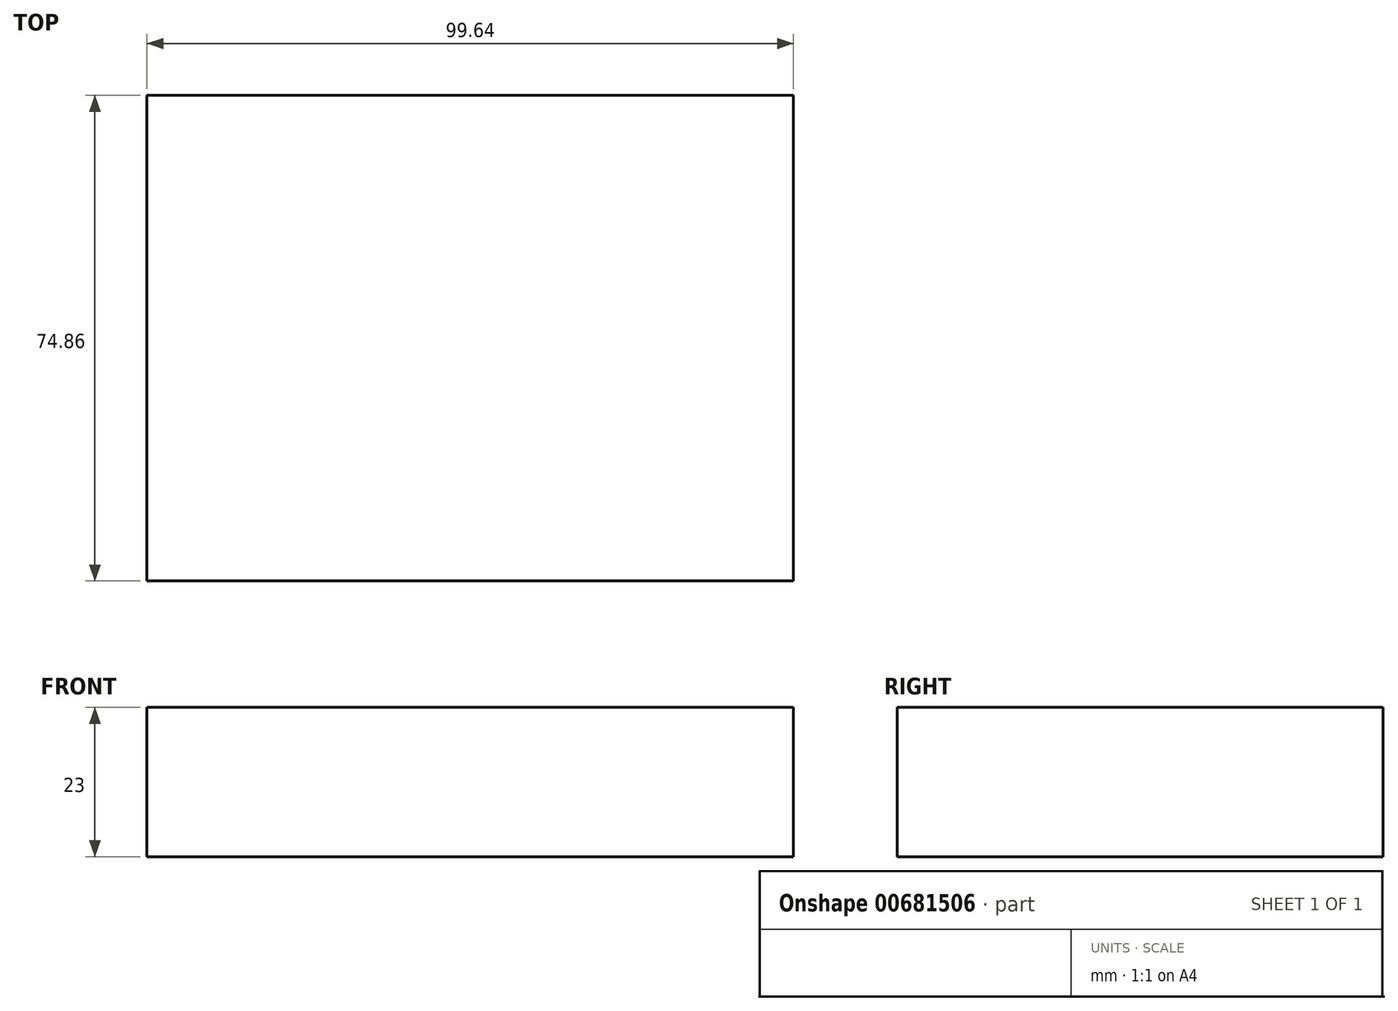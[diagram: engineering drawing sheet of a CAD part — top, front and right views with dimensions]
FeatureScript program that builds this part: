
annotation { "Feature Type Name" : "Feature", "Feature Type Description" : "" }
export const myFeature = defineFeature(function(context is Context, id is Id, definition is map)
    precondition{}
    {
        {
            var Q0;
            Q0=qCreatedBy(makeId("Top.planeOp"),FACE);
            var sketch = newSketch(context, id + "F0", { "sketchPlane" : qUnion([Q0])});
            skLineSegment(sketch, "E0.bottom", {"start": v(-46.68, 37.88) * mm, "end": v(52.96, 37.88) * mm});
            skLineSegment(sketch, "E0.top", {"start": v(-46.68, -36.98) * mm, "end": v(52.96, -36.98) * mm});
            skLineSegment(sketch, "E0.left", {"start": v(-46.68, 37.88) * mm, "end": v(-46.68, -36.98) * mm});
            skLineSegment(sketch, "E0.right", {"start": v(52.96, 37.88) * mm, "end": v(52.96, -36.98) * mm});
            skSolve(sketch);
        }
        {
            var Q0;
            Q0=makeQuery(id+"F0.imprint","IMPRINT",FACE,{"disambiguationData":[TD([[makeQuery(id+"F0.imprint","IMPRINT",EDGE,{"derivedFrom":sQuery(id+"F0.wireOp",EDGE,"E0.bottom")}),-1.0]])]});
            extrude(context, id + "F1", {"entities" : qUnion([Q0]), "depth" : 23 * mm, "offsetDistance" : 25.4 * mm});
        }
    });
